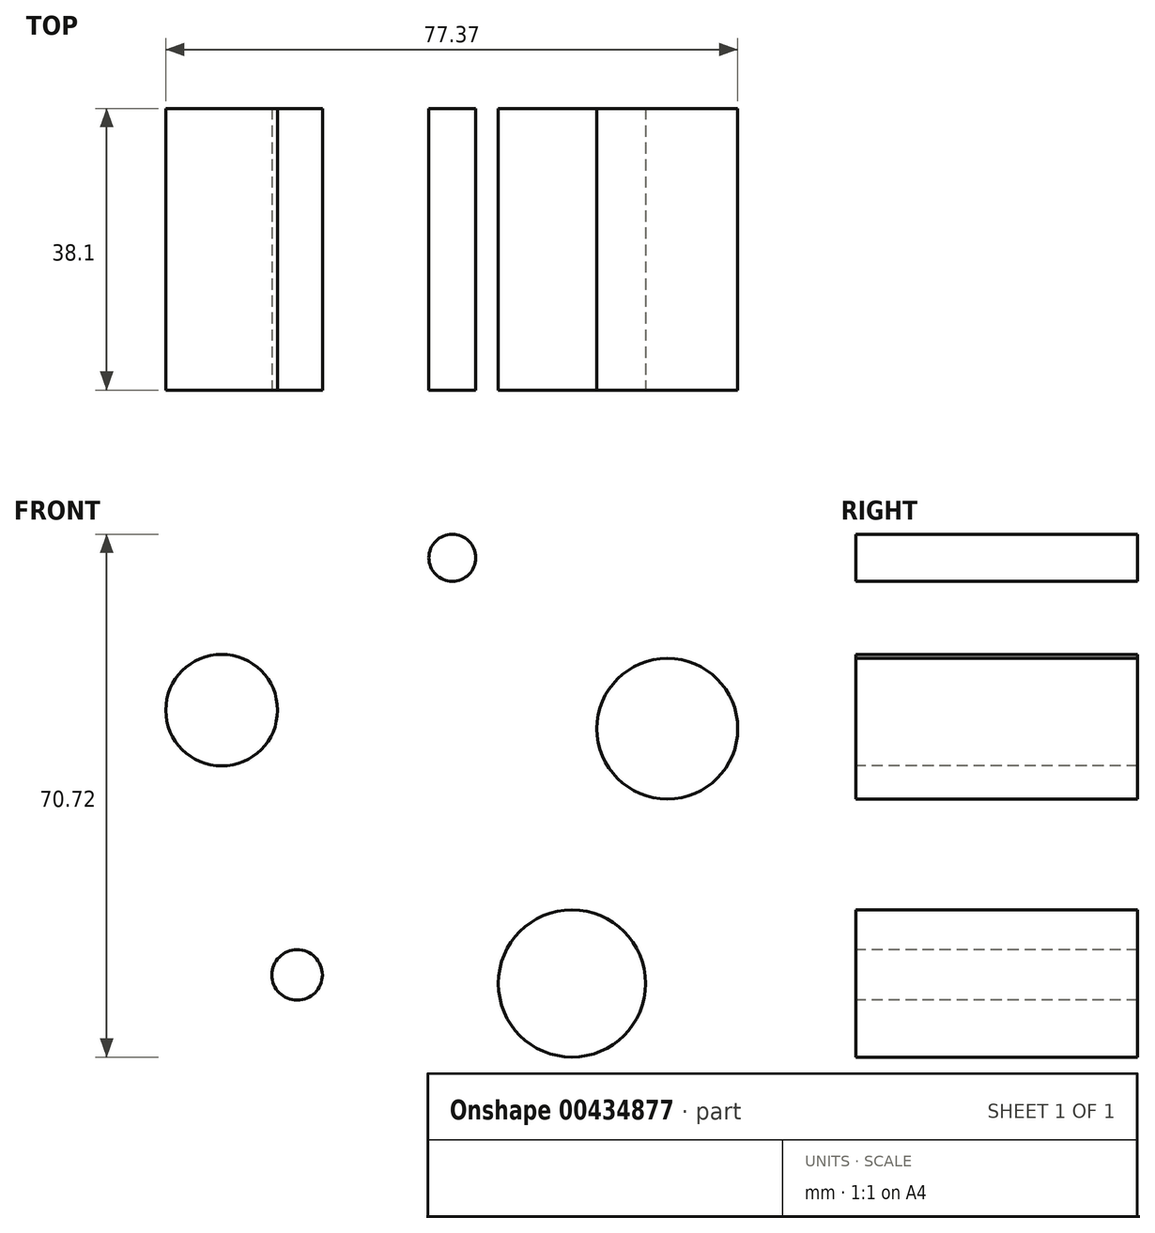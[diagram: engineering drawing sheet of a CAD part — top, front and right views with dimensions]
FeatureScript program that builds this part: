
annotation { "Feature Type Name" : "Feature", "Feature Type Description" : "" }
export const myFeature = defineFeature(function(context is Context, id is Id, definition is map)
    precondition{}
    {
        {
            var Q0;
            Q0=qCreatedBy(makeId("Front.planeOp"),FACE);
            var sketch = newSketch(context, id + "F0", { "sketchPlane" : qUnion([Q0])});
            skCircle(sketch, "E0", {"center": v(-54.66, 27.41) * mm, "radius": 50.8 * mm});
            skCircle(sketch, "E1", {"center": v(-54.66, 27.41) * mm, "radius": 31.75 * mm});
            skSolve(sketch);
        }
        {
            var Q0;
            Q0=makeQuery(id+"F0.imprint","IMPRINT",FACE,{"disambiguationData":[TD([[makeQuery(id+"F0.imprint","IMPRINT",EDGE,{"derivedFrom":sQuery(id+"F0.wireOp",EDGE,"E1")}),1.0]])]});
            var sketch = newSketch(context, id + "F1", { "sketchPlane" : qUnion([Q0])});
            skCircle(sketch, "E2", {"center": v(-53.31, 59.2) * mm, "radius": 3.18 * mm});
            skCircle(sketch, "E3", {"center": v(-24.23, 36.08) * mm, "radius": 9.53 * mm});
            skCircle(sketch, "E4", {"center": v(-84.52, 38.58) * mm, "radius": 7.55 * mm});
            skCircle(sketch, "E5", {"center": v(-74.3, 2.76) * mm, "radius": 3.41 * mm});
            skCircle(sketch, "E6", {"center": v(-37.13, 1.6) * mm, "radius": 4.76 * mm});
            skCircle(sketch, "E7", {"center": v(-37.13, 1.6) * mm, "radius": 9.95 * mm});
            skSolve(sketch);
        }
        {
            var Q0;
            Q0=sQuery(id+"F1.wireOp",EDGE,"E4");
            var Q1;
            Q1=sQuery(id+"F1.wireOp",EDGE,"E5");
            var Q2;
            Q2=sQuery(id+"F1.wireOp",EDGE,"E7");
            var Q3;
            Q3=sQuery(id+"F1.wireOp",EDGE,"E3");
            var Q4;
            Q4=sQuery(id+"F1.wireOp",EDGE,"E2");
            extrude(context, id + "F2", {"bodyType" : ToolBodyType.SURFACE, "surfaceEntities" : qUnion([Q0, Q1, Q2, Q3, Q4]), "depth" : 38.1 * mm});
        }
    });
